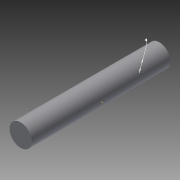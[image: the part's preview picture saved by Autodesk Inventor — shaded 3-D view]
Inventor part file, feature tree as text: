
AUTODESK INVENTOR PART (.ipt)
format: ipt  version: 2015 SP1 (Build 190203100, 203)  size: 77,312 bytes
history: native  units: mm
features: other x3, sketch x2
ambient origin geometry x8: Origin, YZ Plane, XZ Plane, XY Plane, X Axis, Y Axis, Z Axis, Center Point
bodies: Solid1 (feature_tree)
feature tree (5):
  other  "Part3.ipt"
  other  "Solid2::Part3.ipt"
  other  "TaggingFeature1"
  sketch  "Sketch5"  dims[d0=10.0mm]
  sketch  "Sketch7"
